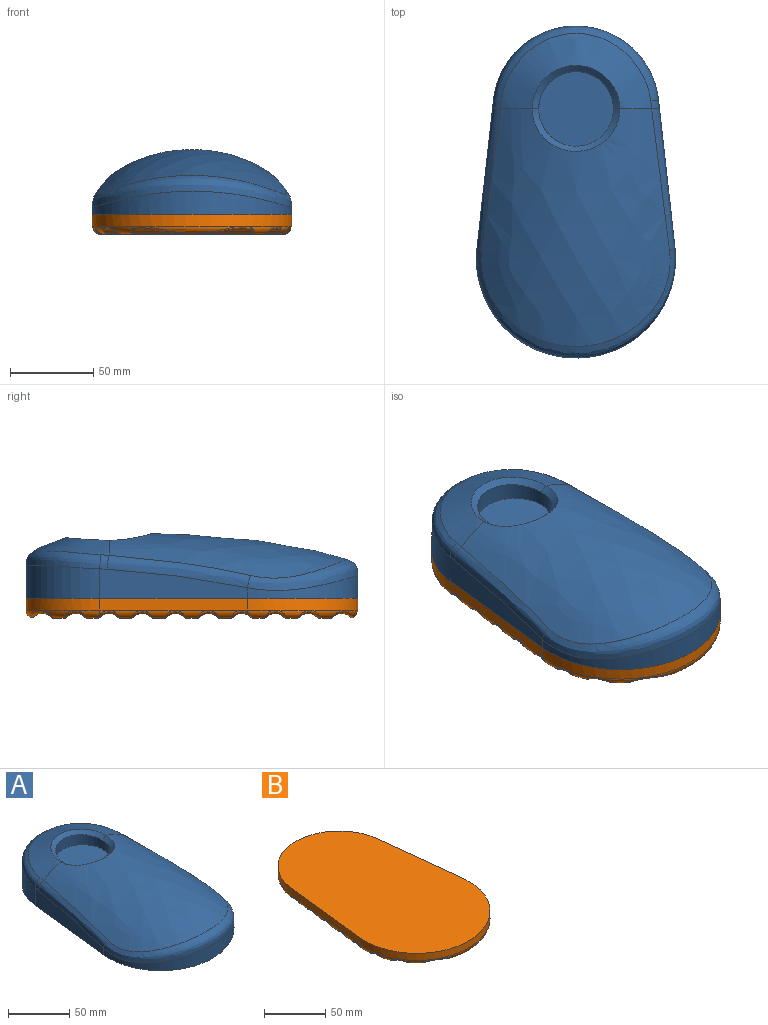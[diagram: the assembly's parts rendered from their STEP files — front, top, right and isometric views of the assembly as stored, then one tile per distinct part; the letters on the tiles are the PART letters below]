
ASSEMBLY  parts=2 mates=1
PART A: 17 faces, bbox 152.1x230.8x87.3 mm
  f0: bspline ~163.3x150mm, area 13980.6mm2, adj f1,f8,f10,f12,f16
  f1: bspline ~150x72.18mm, area 2326.2mm2, adj f0,f9,f11,f13,f15
  f2: plane 90.99x19.89mm, normal (-0.99,0.11,0), area 1184mm2, adj f4,f5,f12,f13,f14
  f3: plane 90.99x19.89mm, normal (0.99,0.11,0), area 1184mm2, adj f4,f5,f8,f9,f14
  f4: cylinder r=50mm len=99.38mm, axis (0,0,-1), area 2596.5mm2, adj f2,f3,f11,f14
  f5: cylinder r=60mm len=120mm, axis (0,0,-1), area 1794.7mm2, adj f2,f3,f10,f14
  f6: cylinder r=22.5mm len=45mm, axis (0,0,-1), area 1300mm2, adj f7,f15,f16
  f7: plane 45x45mm, normal (0,0,1), area 1590.4mm2, adj f6
  f8: bspline ~86.46x19.58mm, area 822.8mm2, adj f0,f3,f9,f10
  f9: bspline ~8.72x5.56mm, area 47.8mm2, adj f1,f3,f8,f11
  f10: bspline ~120.25x66.67mm, area 2099mm2, adj f0,f5,f8,f12
  f11: bspline ~99.43x45.29mm, area 1490.8mm2, adj f1,f4,f9,f13
  f12: bspline ~86.46x19.58mm, area 822.8mm2, adj f0,f2,f10,f13
  f13: bspline ~8.72x5.56mm, area 47.8mm2, adj f1,f2,f11,f12
  f14: plane 200x120mm, normal (0,0,-1), area 19543mm2, adj f2,f3,f4,f5
  f15: bspline ~52.87x26.21mm, area 366.2mm2, adj f1,f6,f16
  f16: bspline ~52.87x25.57mm, area 350.7mm2, adj f0,f6,f15
PART B: 88 faces, bbox 121.2x209.1x12.1 mm
  f0: torus R=45mm, axis (0,0,1), area 97.3mm2, adj f32,f35,f83,f86
  f1: torus R=45mm, axis (0,0,1), area 71.2mm2, adj f25,f30,f35,f81,f84
  f2: torus R=45mm, axis (0,0,1), area 97.3mm2, adj f32,f35,f84,f86
  f3: torus R=45mm, axis (0,0,1), area 163.8mm2, adj f35,f86
  f4: cylinder r=5mm len=20.56mm, axis (0.11,-0.99,0), area 72.5mm2, adj f24,f36,f60,f64
  f5: cylinder r=5mm len=20.56mm, axis (0.11,-0.99,0), area 72.5mm2, adj f27,f36,f64,f68
  f6: cylinder r=5mm len=20.56mm, axis (0.11,-0.99,0), area 72.5mm2, adj f28,f36,f68,f72
  f7: cylinder r=5mm len=20.56mm, axis (0.11,-0.99,0), area 72.5mm2, adj f29,f36,f72,f76
  f8: cylinder r=5mm len=5.42mm, axis (0.11,-0.99,0), area 4.8mm2, adj f31,f36,f76
  f9: cylinder r=5mm len=3.57mm, axis (0.11,0.99,0), area 1.4mm2, adj f21,f37,f63
  f10: cylinder r=5mm len=20.56mm, axis (0.11,0.99,0), area 72.5mm2, adj f24,f37,f63,f67
  f11: cylinder r=5mm len=20.56mm, axis (0.11,0.99,0), area 72.5mm2, adj f27,f37,f67,f71
  f12: cylinder r=5mm len=20.56mm, axis (0.11,0.99,0), area 72.5mm2, adj f28,f37,f71,f75
  f13: cylinder r=5mm len=20.56mm, axis (0.11,0.99,0), area 72.5mm2, adj f29,f37,f75,f79
  f14: torus R=55mm, axis (0,0,1), area 104.6mm2, adj f20,f34,f48,f51
  f15: torus R=55mm, axis (0,0,1), area 178.8mm2, adj f34,f48
  f16: torus R=55mm, axis (0,0,1), area 79mm2, adj f22,f34,f51,f55
  f17: torus R=55mm, axis (0,0,1), area 104.6mm2, adj f20,f34,f48,f52
  f18: torus R=55mm, axis (0,0,1), area 72.5mm2, adj f23,f26,f34,f55,f58
  f19: torus R=55mm, axis (0,0,1), area 79mm2, adj f22,f34,f52,f56
  f20: plane 81.52x6.14mm, normal (0,0,-1), area 462.7mm2, adj f14,f17,f49,f50
  f21: torus R=55mm, axis (0,0,1), area 72.5mm2, adj f9,f23,f34,f56,f61
  f22: plane 104.66x6.14mm, normal (0,0,-1), area 629.1mm2, adj f16,f19,f53,f54
  f23: plane 110x6.14mm, normal (0,0,-1), area 675.4mm2, adj f18,f21,f57,f59
  f24: plane 106.9x6.14mm, normal (0,0,-1), area 652.5mm2, adj f4,f10,f62,f65
  f25: cylinder r=5mm len=5.42mm, axis (0.11,0.99,0), area 4.8mm2, adj f1,f37,f79
  f26: cylinder r=5mm len=3.57mm, axis (0.11,-0.99,0), area 1.4mm2, adj f18,f36,f60
  f27: plane 102.43x6.14mm, normal (0,0,-1), area 625.1mm2, adj f5,f11,f66,f69
  f28: plane 97.96x6.14mm, normal (0,0,-1), area 597.6mm2, adj f6,f12,f70,f73
  f29: plane 93.48x6.14mm, normal (0,0,-1), area 570.1mm2, adj f7,f13,f74,f77
  f30: plane 88.93x6.14mm, normal (0,0,-1), area 538.6mm2, adj f1,f31,f80,f82
  f31: torus R=45mm, axis (0,0,1), area 71.2mm2, adj f8,f30,f35,f78,f83
  f32: plane 72.11x6.14mm, normal (0,0,-1), area 411.1mm2, adj f0,f2,f85,f87
  f33: plane 200x120mm, normal (0,0,1), area 19543mm2, adj f34,f35,f36,f37
  f34: cylinder r=60mm len=120mm, axis (0,0,-1), area 1413mm2, adj f14,f15,f16,f17,f18,f19,f21,f33
  f35: cylinder r=50mm len=99.38mm, axis (0,0,-1), area 1021.6mm2, adj f0,f1,f2,f3,f31,f33,f36,f37
  f36: plane 88.89x9.94mm, normal (0.99,0.11,0), area 626.1mm2, adj f4,f5,f6,f7,f8,f26,f33,f34
  f37: plane 88.89x9.94mm, normal (-0.99,0.11,0), area 626.1mm2, adj f9,f10,f11,f12,f13,f25,f33,f34
  f38: cylinder r=7.5mm len=65.25mm, axis (1,0,0), area 590mm2, adj f86,f87
  f39: cylinder r=7.5mm len=90.44mm, axis (1,0,0), area 1053.1mm2, adj f82,f83,f84,f85
  f40: cylinder r=7.5mm len=97.23mm, axis (1,0,0), area 1174.5mm2, adj f76,f77,f78,f79,f80,f81
  f41: cylinder r=7.5mm len=101.71mm, axis (1,0,0), area 1229.4mm2, adj f72,f73,f74,f75
  f42: cylinder r=7.5mm len=106.18mm, axis (1,0,0), area 1284.2mm2, adj f68,f69,f70,f71
  f43: cylinder r=7.5mm len=110.65mm, axis (1,0,0), area 1339mm2, adj f64,f65,f66,f67
  f44: cylinder r=7.5mm len=115.12mm, axis (1,0,0), area 1393.6mm2, adj f58,f59,f60,f61,f62,f63
  f45: cylinder r=7.5mm len=115.12mm, axis (1,0,0), area 1387.1mm2, adj f54,f55,f56,f57
  f46: cylinder r=7.5mm len=103.91mm, axis (1,0,0), area 1199.6mm2, adj f50,f51,f52,f53
  f47: cylinder r=7.5mm len=72.84mm, axis (1,0,0), area 654.9mm2, adj f48,f49
  f48: bspline ~74.72x14.7mm, area 241.6mm2, adj f14,f15,f17,f47,f49
  f49: cylinder r=2mm len=68.41mm, axis (1,0,0), area 111.8mm2, adj f20,f47,f48
  f50: cylinder r=2mm len=81.52mm, axis (1,0,0), area 133.2mm2, adj f20,f46,f51,f52
  f51: bspline ~14.26x13.54mm, area 55.6mm2, adj f14,f16,f46,f50,f53
  f52: bspline ~14.27x13.62mm, area 55.6mm2, adj f17,f19,f46,f50,f53
  f53: cylinder r=2mm len=99.85mm, axis (1,0,0), area 163.2mm2, adj f22,f46,f51,f52
  f54: cylinder r=2mm len=104.66mm, axis (1,0,0), area 171.1mm2, adj f22,f45,f55,f56
  f55: bspline ~13.93x7.91mm, area 48mm2, adj f16,f18,f45,f54,f57
  f56: bspline ~13.93x7.92mm, area 48mm2, adj f19,f21,f45,f54,f57
  f57: cylinder r=2mm len=109.83mm, axis (1,0,0), area 179.5mm2, adj f23,f45,f55,f56
  f58: bspline ~4.93x4.82mm, area 12.3mm2, adj f18,f44,f59,f60
  f59: cylinder r=2mm len=109.83mm, axis (1,0,0), area 179.5mm2, adj f23,f44,f58,f61
  f60: bspline ~10.45x6.26mm, area 33.2mm2, adj f4,f26,f44,f58,f62
  f61: bspline ~4.93x4.82mm, area 12.3mm2, adj f21,f44,f59,f63
  f62: cylinder r=2mm len=106.9mm, axis (1,0,0), area 174.7mm2, adj f24,f44,f60,f63
  f63: bspline ~10.65x6.87mm, area 33.2mm2, adj f9,f10,f44,f61,f62
  f64: bspline ~13.88x6.76mm, area 45.1mm2, adj f4,f5,f43,f65,f66
  f65: cylinder r=2mm len=105.53mm, axis (1,0,0), area 172.5mm2, adj f24,f43,f64,f67
  f66: cylinder r=2mm len=102.43mm, axis (1,0,0), area 167.4mm2, adj f27,f43,f64,f67
  f67: bspline ~13.88x6.87mm, area 45.1mm2, adj f10,f11,f43,f65,f66
  f68: bspline ~13.88x6.76mm, area 45.1mm2, adj f5,f6,f42,f69,f70
  f69: cylinder r=2mm len=101.05mm, axis (1,0,0), area 165.2mm2, adj f27,f42,f68,f71
  f70: cylinder r=2mm len=97.96mm, axis (1,0,0), area 160.1mm2, adj f28,f42,f68,f71
  f71: bspline ~13.88x6.87mm, area 45.1mm2, adj f11,f12,f42,f69,f70
  f72: bspline ~13.88x6.76mm, area 45.1mm2, adj f6,f7,f41,f73,f74
  f73: cylinder r=2mm len=96.58mm, axis (1,0,0), area 157.9mm2, adj f28,f41,f72,f75
  f74: cylinder r=2mm len=93.48mm, axis (1,0,0), area 152.8mm2, adj f29,f41,f72,f75
  f75: bspline ~13.88x6.87mm, area 45.1mm2, adj f12,f13,f41,f73,f74
  f76: bspline ~13.09x5.43mm, area 36.7mm2, adj f7,f8,f40,f77,f78
  f77: cylinder r=2mm len=92.11mm, axis (1,0,0), area 150.6mm2, adj f29,f40,f76,f79
  f78: bspline ~5.88x3.63mm, area 8.6mm2, adj f31,f40,f76,f80
  f79: bspline ~13.09x5.41mm, area 36.7mm2, adj f13,f25,f40,f77,f81
  f80: cylinder r=2mm len=88.93mm, axis (1,0,0), area 145.4mm2, adj f30,f40,f78,f81
  f81: bspline ~5.88x3.63mm, area 8.6mm2, adj f1,f40,f79,f80
  f82: cylinder r=2mm len=86.12mm, axis (1,0,0), area 140.8mm2, adj f30,f39,f83,f84
  f83: bspline ~14.15x11.43mm, area 52.9mm2, adj f0,f31,f39,f82,f85
  f84: bspline ~14.15x11.07mm, area 52.9mm2, adj f1,f2,f39,f82,f85
  f85: cylinder r=2mm len=72.11mm, axis (1,0,0), area 117.9mm2, adj f32,f39,f83,f84
  f86: bspline ~67.35x14.66mm, area 222.1mm2, adj f0,f2,f3,f38,f87
  f87: cylinder r=2mm len=61.03mm, axis (1,0,0), area 99.8mm2, adj f32,f38,f86
PLACE A t=(57.89,47.28,-168.58)mm
PLACE B t=(57.89,47.28,-168.58)mm
MATE fastened A.f14 <-> B.f33  axis (0,0,-1) through (157.89,-5.49,-156.58)mm
